# Revit family: Curved Walls L-Bend Finished Edge
name_source: partatom
category: Generic Models
revit_build: Autodesk Revit 2016 (Build: 20150714_1515(x64)
units: mm (PartAtom-declared; Revit-internal decimal feet)

## family parameters
Always vertical = No
Can host rebar = No
Cut with Voids When Loaded = No
Part Type = Normal
Room Calculation Point = No
Round Connector Dimension = Use Diameter
Shared = No
Work Plane-Based = Yes

## types (2) — shared parameters
Default Elevation = 0' - 0"
Description = Prefabricated Drywall Profiles
GWB Thickness (1/2" or 5/8") = 0' - 0 1/2"
Manufacturer = Curved Walls Inc
URL = www.curvedwalls.ca

## per-type parameters (varying)
| type | A Shelf Width (Min 2" Max 12" Without additional reinforcement) | B - Exposed Edge Height (Min 1") | C Edge Return |
| 1/2" Thk. x 8" W x 2" EH x 2" ER | 0' - 8" | 0' - 2" | 0' - 2" |
| 5/8" Thk. x 6" W x 3" EH x 1" ER | 0' - 6" | 0' - 1" | 0' - 1" |

## geometry (parser evidence)
native form markers: Blend x4, Sweep x2
no freeform markers — native parametric forms only
